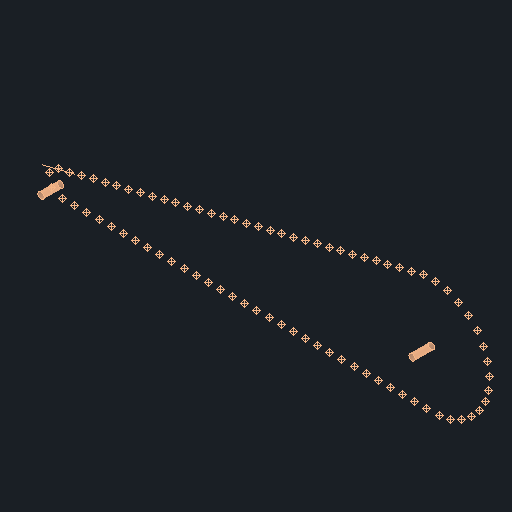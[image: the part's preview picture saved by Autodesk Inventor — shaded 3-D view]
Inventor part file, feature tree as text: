
AUTODESK INVENTOR PART (.ipt)
format: ipt  version: 2023 (Build 270158000, 158)  size: 123,904 bytes
history: native  units: in
note: dims shown in document units (in); Inventor stores cm internally (conversion verified against a paired STEP export)
features: other x83, sketch x3, extrude x2, pattern_linear x1
ambient origin geometry x8: Origin, YZ Plane, XZ Plane, XY Plane, X Axis, Y Axis, Z Axis, Center Point
bodies: Body1 (feature_tree), Body2 (feature_tree)
feature tree (89):
  sketch  "Sketch1"  dims[d3=31.6185in]
  other  "Work Point1"
  pattern_linear  "Rectangular Pattern1"  Spacing1=1.1156in  [1 undecoded]
  other  "Work Axis1"
  other  "Work Point2"
  other  "Work Point3"
  other  "Work Point4"
  other  "Work Point5"
  other  "Work Point6"
  other  "Work Point7"
  other  "Work Point8"
  other  "Work Point9"
  other  "Work Point10"
  other  "Work Point50"
  other  "Work Point51"
  other  "Work Point52"
  other  "Work Point53"
  other  "Work Point54"
  other  "Work Point55"
  other  "Work Point56"
  other  "Work Point57"
  other  "Work Point58"
  other  "Work Point59"
  other  "Work Point60"
  other  "Work Point61"
  other  "Work Point62"
  other  "Work Point63"
  other  "Work Point64"
  other  "Work Point65"
  other  "Work Point66"
  other  "Work Point67"
  other  "Work Point68"
  other  "Work Point69"
  other  "Work Point70"
  other  "Work Point71"
  other  "Work Point72"
  other  "Work Point73"
  other  "Work Point74"
  other  "Work Point75"
  other  "Work Point76"
  other  "Work Point77"
  other  "Work Point78"
  other  "Work Point79"
  other  "Work Point80"
  other  "Work Point81"
  other  "Work Point82"
  other  "Work Point83"
  sketch  "Sketch2"  dims[d5=11.9109in]
  other  "Srf1"
  sketch  "Sketch3"  dims[d6=11.9109in d7=1.1156in d8=6.2463in d9=0.2in d10=0.625in d11=0.0in d12=0.2in d13=0.625in d14=0.0in]
  other  "Srf2"
  other  "Work Point97"
  other  "Work Point98"
  other  "Work Point99"
  other  "Work Point100"
  other  "Work Point101"
  other  "Work Point102"
  other  "Work Point103"
  other  "Work Point104"
  other  "Work Point105"
  other  "Work Point106"
  other  "Work Point107"
  other  "Work Point108"
  other  "Work Point109"
  other  "Work Point110"
  other  "Work Point111"
  other  "Work Point112"
  other  "Work Point113"
  other  "Work Point114"
  other  "Work Point123"
  other  "Work Point124"
  other  "Work Point125"
  other  "Work Point126"
  other  "Work Point127"
  other  "Work Point128"
  other  "Work Point129"
  other  "Work Point130"
  other  "Work Point131"
  other  "Work Point132"
  other  "Work Point133"
  other  "Work Point134"
  other  "Work Point135"
  other  "Work Point136"
  other  "Work Point137"
  other  "Work Point138"
  other  "Work Point139"
  other  "Work Point140"
  extrude  "ExtrusionSrf1"  Depth=6.2463in
  extrude  "ExtrusionSrf2"  Depth=0.2in
note: 1 required parameter value undecoded (feature->parameter linkage not recoverable at this tier; creation-order binding heuristic only, values carry confidence <= 0.55)
